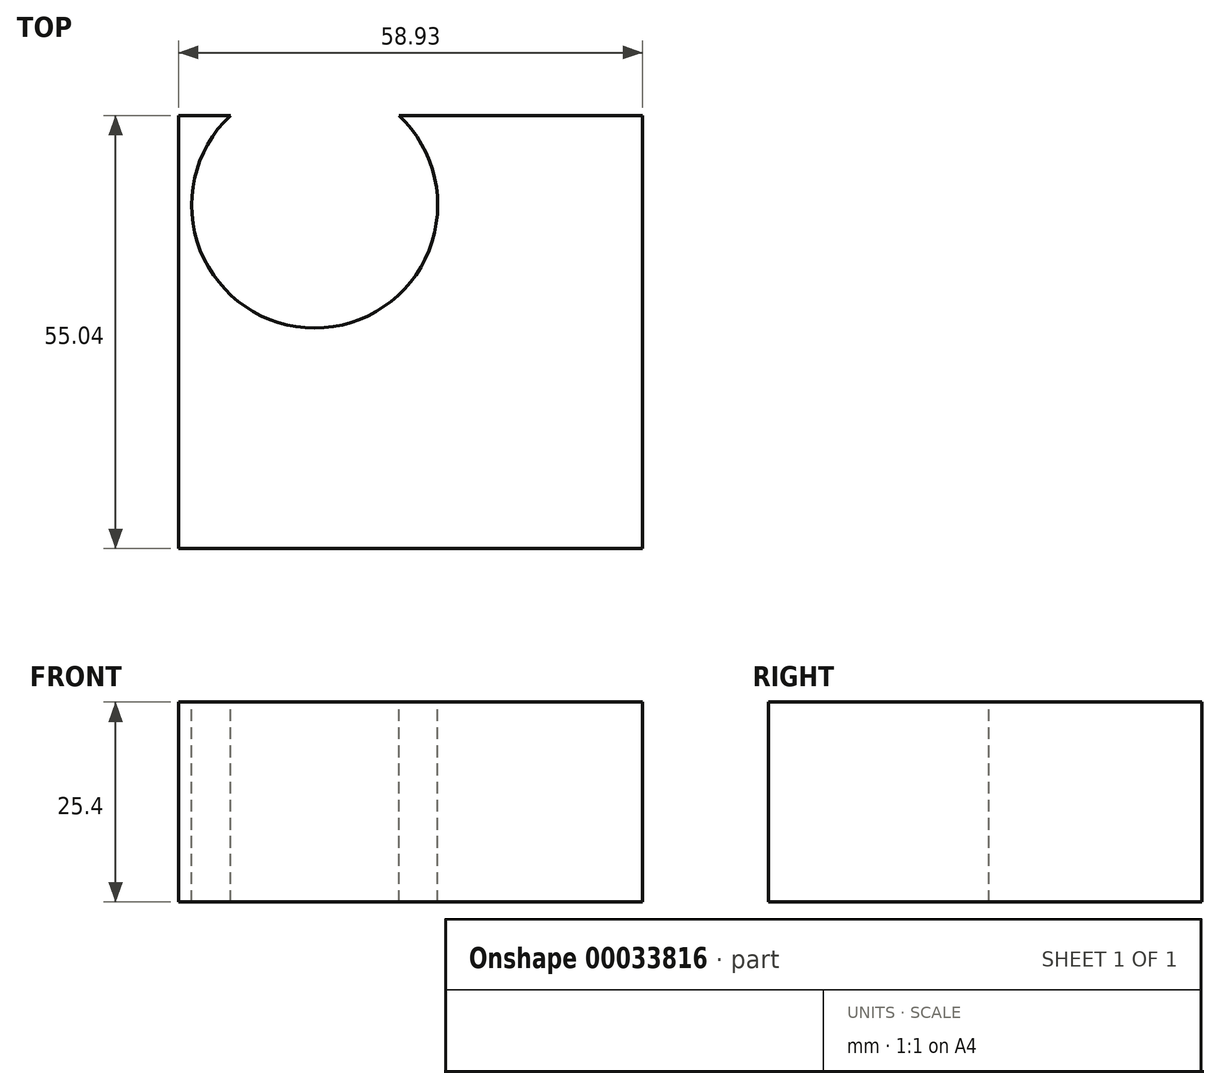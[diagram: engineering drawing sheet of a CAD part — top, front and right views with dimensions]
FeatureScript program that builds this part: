
annotation { "Feature Type Name" : "Feature", "Feature Type Description" : "" }
export const myFeature = defineFeature(function(context is Context, id is Id, definition is map)
    precondition{}
    {
        {
            var Q0;
            Q0=qCreatedBy(makeId("Top.planeOp"),FACE);
            var sketch = newSketch(context, id + "F0", { "sketchPlane" : qUnion([Q0])});
            skLineSegment(sketch, "E0.bottom", {"start": v(-58.93, 30.98) * mm, "end": v(0, 30.98) * mm});
            skLineSegment(sketch, "E0.top", {"start": v(-58.93, -24.06) * mm, "end": v(0, -24.06) * mm});
            skLineSegment(sketch, "E0.left", {"start": v(-58.93, 30.98) * mm, "end": v(-58.93, -24.06) * mm});
            skLineSegment(sketch, "E0.right", {"start": v(0, 30.98) * mm, "end": v(0, -24.06) * mm});
            skSolve(sketch);
        }
        {
            var Q0;
            Q0=makeQuery(id+"F0.imprint","IMPRINT",FACE,{"disambiguationData":[TD([[makeQuery(id+"F0.imprint","IMPRINT",EDGE,{"derivedFrom":sQuery(id+"F0.wireOp",EDGE,"E0.bottom")}),-1.0]])]});
            extrude(context, id + "F1", {"entities" : qUnion([Q0]), "depth" : 25.4 * mm});
        }
        {
            var Q0;
            Q0=makeQuery(id+"F1.opExtrude","CAP_FACE",FACE,{"disambiguationData":[OSD([sQuery(id+"F0.wireOp",EDGE,"E0.bottom"),sQuery(id+"F0.wireOp",EDGE,"E0.top"),sQuery(id+"F0.wireOp",EDGE,"E0.left"),sQuery(id+"F0.wireOp",EDGE,"E0.right")])],"isStart":false});
            var sketch = newSketch(context, id + "F2", { "sketchPlane" : qUnion([Q0])});
            skCircle(sketch, "E1", {"center": v(-41.64, 19.6) * mm, "radius": 15.62 * mm});
            skCircle(sketch, "E2", {"center": v(34.06, -40.18) * mm, "radius": 98.78 * mm});
            skSolve(sketch);
        }
        {
            var Q0;
            {var subQ1=sQuery(id+"F2.wireOp",EDGE,"E2");var subQ3=sQuery(id+"F2.wireOp",EDGE,"E1");var subQ5=makeQuery(id+"F2.imprint","INTERSECT",VERTEX,{"disambiguationData":[OD(1.0)],"derivedFrom":[subQ3,subQ1]});Q0=makeQuery(id+"F2.imprint","IMPRINT",FACE,{"disambiguationData":[TD([[makeQuery(id+"F2.imprint","IMPRINT",EDGE,{"disambiguationData":[TD([[subQ5,-1.0]])],"derivedFrom":subQ3}),1.0]])]});}
            var Q1;
            {var subQ1=sQuery(id+"F2.wireOp",EDGE,"E2");var subQ3=sQuery(id+"F2.wireOp",EDGE,"E1");var subQ5=makeQuery(id+"F2.imprint","INTERSECT",VERTEX,{"disambiguationData":[OD(1.0)],"derivedFrom":[subQ3,subQ1]});Q1=makeQuery(id+"F2.imprint","IMPRINT",FACE,{"disambiguationData":[TD([[makeQuery(id+"F2.imprint","IMPRINT",EDGE,{"disambiguationData":[TD([[subQ5,1.0]])],"derivedFrom":subQ3}),1.0]])]});}
            var Q2;
            {var subQ1=sQuery(id+"F2.wireOp",EDGE,"E2");var subQ3=sQuery(id+"F2.wireOp",EDGE,"E1");var subQ5=makeQuery(id+"F2.imprint","INTERSECT",VERTEX,{"disambiguationData":[OD(0.0)],"derivedFrom":[subQ3,subQ1]});Q2=makeQuery(id+"F2.imprint","IMPRINT",FACE,{"disambiguationData":[TD([[makeQuery(id+"F2.imprint","IMPRINT",EDGE,{"disambiguationData":[TD([[subQ5,-1.0]])],"derivedFrom":subQ3}),1.0]])]});}
            extrude(context, id + "F3", {"entities" : qUnion([Q0, Q1, Q2]), "operationType" : NewBodyOperationType.REMOVE, "oppositeDirection" : true, "depth" : 34.69 * mm});
        }
    });
